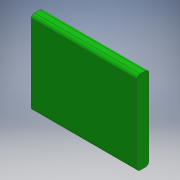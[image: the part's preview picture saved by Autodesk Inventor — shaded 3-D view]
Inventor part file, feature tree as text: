
AUTODESK INVENTOR PART (.ipt)
format: ipt  version: 2018 (Build 220112000, 112)  size: 104,960 bytes
history: native  units: mm
features: extrude x1, fillet x1, sketch x1
ambient origin geometry x8: Origin, YZ Plane, XZ Plane, XY Plane, X Axis, Y Axis, Z Axis, Center Point
bodies: Solid1 (feature_tree)
feature tree (3):
  extrude  "Extrusion1"  Depth=60.96mm
  fillet  "Fillet1"  Radius=7.0mm
  sketch  "Sketch1"  dims[d0=48.15mm d1=60.96mm d2=7.0mm d3=0.0mm d4=2.0mm]
